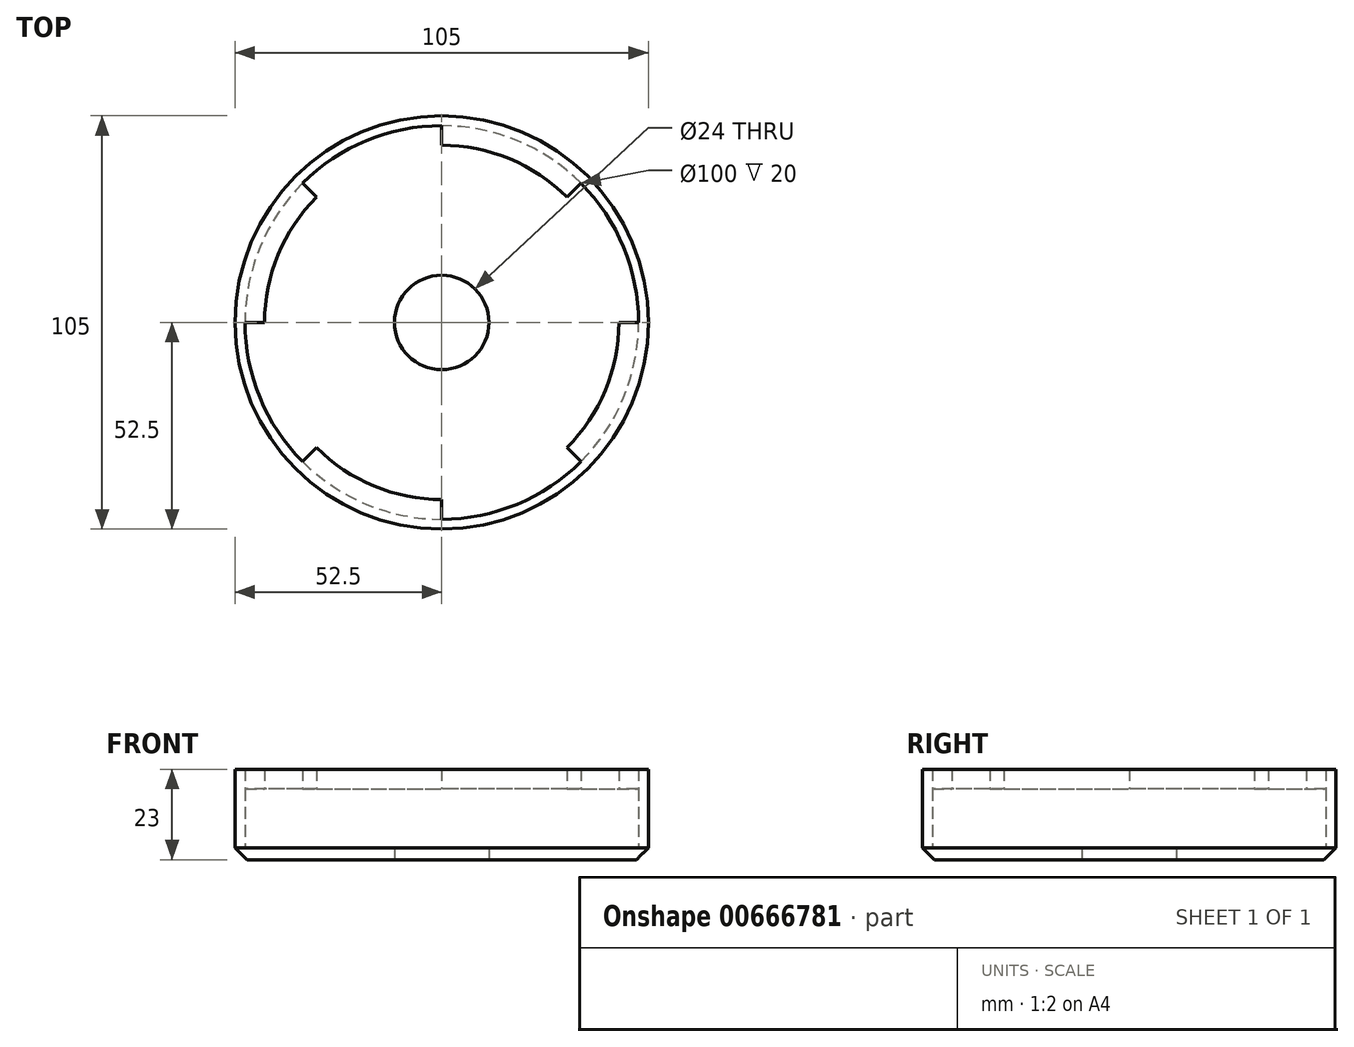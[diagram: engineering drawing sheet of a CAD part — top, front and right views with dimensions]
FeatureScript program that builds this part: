
annotation { "Feature Type Name" : "Feature", "Feature Type Description" : "" }
export const myFeature = defineFeature(function(context is Context, id is Id, definition is map)
    precondition{}
    {
        {
            var Q0;
            Q0=qCreatedBy(makeId("Top.planeOp"),FACE);
            var sketch = newSketch(context, id + "F0", { "sketchPlane" : qUnion([Q0])});
            skCircle(sketch, "E0", {"center": v(0, 0) * mm, "radius": 12 * mm});
            skCircle(sketch, "E1", {"center": v(0, 0) * mm, "radius": 50 * mm});
            skCircle(sketch, "E2", {"center": v(0, 0) * mm, "radius": 52.5 * mm});
            skLineSegment(sketch, "E3", {"start": v(0, -52.5) * mm, "end": v(0, -50) * mm});
            skSolve(sketch);
        }
        {
            var Q0;
            Q0=makeQuery(id+"F0.imprint","IMPRINT",FACE,{"disambiguationData":[TD([[makeQuery(id+"F0.imprint","IMPRINT",EDGE,{"derivedFrom":sQuery(id+"F0.wireOp",EDGE,"E0")}),-1.0]])]});
            extrude(context, id + "F1", {"entities" : qUnion([Q0]), "depth" : 3 * mm, "offsetDistance" : 25 * mm});
        }
        {
            var Q0;
            Q0=makeQuery(id+"F0.imprint","IMPRINT",FACE,{"disambiguationData":[TD([[makeQuery(id+"F0.imprint","IMPRINT",EDGE,{"derivedFrom":sQuery(id+"F0.wireOp",EDGE,"E1")}),-1.0]])]});
            extrude(context, id + "F2", {"entities" : qUnion([Q0]), "operationType" : NewBodyOperationType.ADD, "depth" : 23 * mm, "offsetDistance" : 25 * mm});
        }
        {
            var Q0;
            Q0=qCreatedBy(makeId("Top.planeOp"),FACE);
            var sketch = newSketch(context, id + "F3", { "sketchPlane" : qUnion([Q0])});
            skArc(sketch, "E4", {"start": v(35.36, -35.36) * mm, "mid": v(46.2, -19.13) * mm, "end": v(50, 0) * mm});
            skArc(sketch, "E5", {"start": v(-31.82, 31.82) * mm, "mid": v(-41.57, 17.22) * mm, "end": v(-45, 0) * mm});
            skLineSegment(sketch, "E6", {"start": v(0, 50) * mm, "end": v(0, 45) * mm});
            skLineSegment(sketch, "E7.1.0", {"start": v(-35.36, 35.36) * mm, "end": v(-31.82, 31.82) * mm});
            skLineSegment(sketch, "E7.2.0", {"start": v(-50, 0) * mm, "end": v(-45, 0) * mm});
            skLineSegment(sketch, "E7.3.0", {"start": v(-35.36, -35.36) * mm, "end": v(-31.82, -31.82) * mm});
            skLineSegment(sketch, "E7.4.0", {"start": v(0, -50) * mm, "end": v(0, -45) * mm});
            skLineSegment(sketch, "E7.5.0", {"start": v(35.36, -35.36) * mm, "end": v(31.82, -31.82) * mm});
            skLineSegment(sketch, "E7.6.0", {"start": v(50, 0) * mm, "end": v(45, 0) * mm});
            skLineSegment(sketch, "E7.7.0", {"start": v(35.36, 35.36) * mm, "end": v(31.82, 31.82) * mm});
            skArc(sketch, "E8", {"start": v(0, 50) * mm, "mid": v(19.13, 46.2) * mm, "end": v(35.36, 35.36) * mm});
            skArc(sketch, "E9", {"start": v(-35.36, 35.36) * mm, "mid": v(-46.2, 19.13) * mm, "end": v(-50, 0) * mm});
            skArc(sketch, "E10.trimOffspring", {"start": v(-31.82, -31.82) * mm, "mid": v(-17.22, -41.57) * mm, "end": v(0, -45) * mm});
            skArc(sketch, "E11.trimOffspring", {"start": v(31.82, -31.82) * mm, "mid": v(41.57, -17.22) * mm, "end": v(45, 0) * mm});
            skArc(sketch, "E12.trimOffspring", {"start": v(-35.36, -35.36) * mm, "mid": v(-19.13, -46.2) * mm, "end": v(0, -50) * mm});
            skArc(sketch, "E13.trimOffspring", {"start": v(50, 0) * mm, "mid": v(46.2, -19.13) * mm, "end": v(35.36, -35.36) * mm});
            skArc(sketch, "E14.trimOffspring", {"start": v(31.82, 31.82) * mm, "mid": v(17.22, 41.57) * mm, "end": v(0, 45) * mm});
            skArc(sketch, "E15.trimOffspring", {"start": v(35.36, 35.36) * mm, "mid": v(19.13, 46.2) * mm, "end": v(0, 50) * mm});
            skArc(sketch, "E16.trimOffspring", {"start": v(0, -50) * mm, "mid": v(-19.13, -46.2) * mm, "end": v(-35.36, -35.36) * mm});
            skSolve(sketch);
        }
        {
            var Q0;
            Q0=qSketchRegion(id+"F3",true);
            extrude(context, id + "F4", {"entities" : qUnion([Q0]), "operationType" : NewBodyOperationType.ADD, "depth" : 23 * mm, "offsetDistance" : 25 * mm, "hasSecondDirection" : true, "secondDirectionOppositeDirection" : true, "secondDirectionDepth" : -18 * mm});
        }
        {
            var Q0;
            Q0=makeQuery(id+"F2.opExtrude","CAP_EDGE",EDGE,{"disambiguationData":[OSD([sQuery(id+"F0.wireOp",EDGE,"E2")])],"isStart":true});
            chamfer(context, id + "F5", {"entities" : qUnion([Q0]), "width" : 3 * mm, "tangentPropagation" : true});
        }
    });
